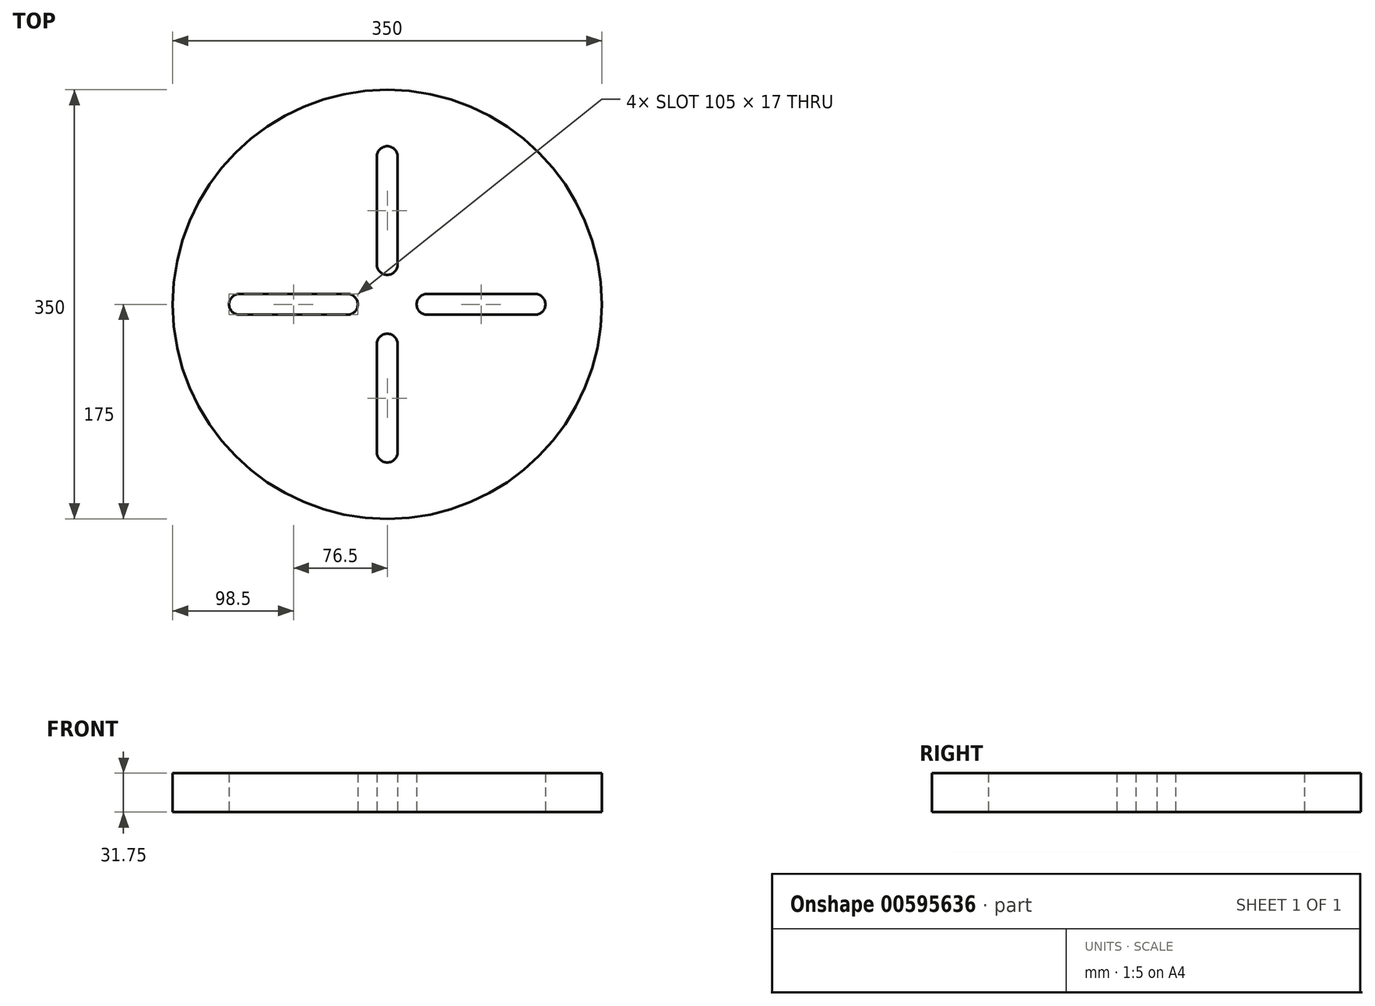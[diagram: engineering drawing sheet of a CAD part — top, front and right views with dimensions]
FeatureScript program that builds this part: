
annotation { "Feature Type Name" : "Feature", "Feature Type Description" : "" }
export const myFeature = defineFeature(function(context is Context, id is Id, definition is map)
    precondition{}
    {
        {
            var Q0;
            Q0=qCreatedBy(makeId("Top.planeOp"),FACE);
            var sketch = newSketch(context, id + "F0", { "sketchPlane" : qUnion([Q0])});
            skCircle(sketch, "E0", {"center": v(0, 0) * mm, "radius": 175 * mm});
            skLineSegment(sketch, "E1.bottom", {"start": v(0, 129) * mm, "end": v(0, 129) * mm});
            skLineSegment(sketch, "E1.top", {"start": v(0, 24) * mm, "end": v(0, 24) * mm});
            skLineSegment(sketch, "E1.left", {"start": v(-8.5, 120.5) * mm, "end": v(-8.5, 32.5) * mm});
            skLineSegment(sketch, "E1.right", {"start": v(8.5, 120.5) * mm, "end": v(8.5, 32.5) * mm});
            skPoint(sketch, "E2.visualSharp", {"position": v(-8.5, 129) * mm});
            skArc(sketch, "E2.filletArc", {"start": v(0, 129) * mm, "mid": v(-6.01, 126.51) * mm, "end": v(-8.5, 120.5) * mm});
            skPoint(sketch, "E3.visualSharp", {"position": v(8.5, 129) * mm});
            skArc(sketch, "E3.filletArc", {"start": v(8.5, 120.5) * mm, "mid": v(6.01, 126.51) * mm, "end": v(0, 129) * mm});
            skPoint(sketch, "E4.visualSharp", {"position": v(8.5, 24) * mm});
            skArc(sketch, "E4.filletArc", {"start": v(0, 24) * mm, "mid": v(6.01, 26.49) * mm, "end": v(8.5, 32.5) * mm});
            skPoint(sketch, "E5.visualSharp", {"position": v(-8.5, 24) * mm});
            skArc(sketch, "E5.filletArc", {"start": v(-8.5, 32.5) * mm, "mid": v(-6.01, 26.49) * mm, "end": v(0, 24) * mm});
            skPoint(sketch, "E6.1.0", {"position": v(-24, 8.5) * mm});
            skPoint(sketch, "E6.1.1", {"position": v(-24, -8.5) * mm});
            skLineSegment(sketch, "E6.1.2", {"start": v(-120.5, 8.5) * mm, "end": v(-32.5, 8.5) * mm});
            skLineSegment(sketch, "E6.1.3", {"start": v(-120.5, -8.5) * mm, "end": v(-32.5, -8.5) * mm});
            skPoint(sketch, "E6.1.4", {"position": v(-129, -8.5) * mm});
            skPoint(sketch, "E6.1.5", {"position": v(-129, 8.5) * mm});
            skArc(sketch, "E6.1.6", {"start": v(-32.5, -8.5) * mm, "mid": v(-26.49, -6.01) * mm, "end": v(-24, 0) * mm});
            skArc(sketch, "E6.1.7", {"start": v(-24, 0) * mm, "mid": v(-26.49, 6.01) * mm, "end": v(-32.5, 8.5) * mm});
            skArc(sketch, "E6.1.8", {"start": v(-120.5, 8.5) * mm, "mid": v(-126.51, 6.01) * mm, "end": v(-129, 0) * mm});
            skArc(sketch, "E6.1.9", {"start": v(-129, 0) * mm, "mid": v(-126.51, -6.01) * mm, "end": v(-120.5, -8.5) * mm});
            skPoint(sketch, "E6.2.0", {"position": v(-8.5, -24) * mm});
            skPoint(sketch, "E6.2.1", {"position": v(8.5, -24) * mm});
            skLineSegment(sketch, "E6.2.2", {"start": v(-8.5, -120.5) * mm, "end": v(-8.5, -32.5) * mm});
            skLineSegment(sketch, "E6.2.3", {"start": v(8.5, -120.5) * mm, "end": v(8.5, -32.5) * mm});
            skPoint(sketch, "E6.2.4", {"position": v(8.5, -129) * mm});
            skPoint(sketch, "E6.2.5", {"position": v(-8.5, -129) * mm});
            skArc(sketch, "E6.2.6", {"start": v(8.5, -32.5) * mm, "mid": v(6.01, -26.49) * mm, "end": v(0, -24) * mm});
            skArc(sketch, "E6.2.7", {"start": v(0, -24) * mm, "mid": v(-6.01, -26.49) * mm, "end": v(-8.5, -32.5) * mm});
            skArc(sketch, "E6.2.8", {"start": v(-8.5, -120.5) * mm, "mid": v(-6.01, -126.51) * mm, "end": v(0, -129) * mm});
            skArc(sketch, "E6.2.9", {"start": v(0, -129) * mm, "mid": v(6.01, -126.51) * mm, "end": v(8.5, -120.5) * mm});
            skPoint(sketch, "E6.3.0", {"position": v(24, -8.5) * mm});
            skPoint(sketch, "E6.3.1", {"position": v(24, 8.5) * mm});
            skLineSegment(sketch, "E6.3.2", {"start": v(120.5, -8.5) * mm, "end": v(32.5, -8.5) * mm});
            skLineSegment(sketch, "E6.3.3", {"start": v(120.5, 8.5) * mm, "end": v(32.5, 8.5) * mm});
            skPoint(sketch, "E6.3.4", {"position": v(129, 8.5) * mm});
            skPoint(sketch, "E6.3.5", {"position": v(129, -8.5) * mm});
            skArc(sketch, "E6.3.6", {"start": v(32.5, 8.5) * mm, "mid": v(26.49, 6.01) * mm, "end": v(24, 0) * mm});
            skArc(sketch, "E6.3.7", {"start": v(24, 0) * mm, "mid": v(26.49, -6.01) * mm, "end": v(32.5, -8.5) * mm});
            skArc(sketch, "E6.3.8", {"start": v(120.5, -8.5) * mm, "mid": v(126.51, -6.01) * mm, "end": v(129, 0) * mm});
            skArc(sketch, "E6.3.9", {"start": v(129, 0) * mm, "mid": v(126.51, 6.01) * mm, "end": v(120.5, 8.5) * mm});
            skSolve(sketch);
        }
        {
            var Q0;
            Q0=makeQuery(id+"F0.imprint","IMPRINT",FACE,{"disambiguationData":[TD([[makeQuery(id+"F0.imprint","IMPRINT",EDGE,{"derivedFrom":sQuery(id+"F0.wireOp",EDGE,"E0")}),1.0]])]});
            extrude(context, id + "F1", {"entities" : qUnion([Q0]), "depth" : 31.75 * mm, "offsetDistance" : 25 * mm});
        }
    });
